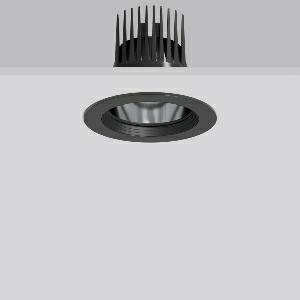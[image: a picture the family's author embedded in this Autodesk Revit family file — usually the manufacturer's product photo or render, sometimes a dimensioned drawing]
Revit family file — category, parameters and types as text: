
# Revit family: heledon_maxi_e_901787_003_2_76_4586
name_source: partatom
category: Lighting Fixtures
units: mm (PartAtom-declared; Revit-internal decimal feet)

## family parameters
Cut with Voids When Loaded = No
Host = Face
Light Source = No
Part Type = Normal
Room Calculation Point = No
Round Connector Dimension = Use Diameter
Shared = No

## types (1)
- HELEDON maxi E (1 x LED Modul 927 bakery, 3300 lm, 2700)
    Apparent Load = 33 VA
    Approval mark = CE
    CIE Flux Codes = 96 100 100 100 100
    Color Rendering = 90
    Color Temperature = 2700
    Default Elevation = 1800 mm
    Description = Series: HELEDON maxi
Round recessed downlight. Housing: die-cast aluminium, powder-coated. Black plastic ring and recessed LED to prevent glare from the side. Optical assembly with reflector made of MIRO-Silver with 98% total light reflection for outstanding efficiency - can be changed without tools. Special LED for illumination of pastries included. Suitable for Recessed ceiling mounting. Installation without tools thanks to spring fastening system. Including separate LED converter with connecting cable 600 mm.High quality converter without flickering and stroboscopic effect. Through-wiring box (5 pole) available as accessory. The following accessories can be mounted without use of tools: interchangeable lenses, decorative glasses, honeycomb louvre, clear and frosted diffusers, white interchangeable plastic ring. 
Colour: deep black, matt (RAL 9005)
Diameter: 162 mm
Height: 3 mm
Cut-out diameter: 152 mm
Recess height: 200 mm
Luminaire: recess height: 135 mm
Lamp: LED
Socket: without socket
Colour temperature: bakery
Colour rendering index (CRI): 97
System power: 33 W
Rated luminous flux: 3300 lm
Luminous efficiency: 100 lm/W
Control gear: Converter, dimmable, DALI
Protection class: II
Type of protection: IP 20
    Height = 0 mm  [stored 0 ft]
    Lamp = 1 x LED Modul 927 bakery
    Lamp Light Flux = 3300 lm
    Lamp count = 1
    Length = 162 mm
    Lifetime = 50000 h
    Luminous efficacy = 100 lm/W
    Manufacturer = RZB
    ModVariant = No
    Model = 901787.003.2.76
    Mounting Place = Ceiling
    Mounting Type = Recessed
    Number of Poles = 1
    OnlyDefault = Yes
    Power Factor = 1
    Product Name = HELEDON maxi E
    Product group = Recessed downlights
    ProductGroupID = 402
    Protection Class = Protection class II
    Protection Degree = IP 20
    RLX_Detail_Level = 1
    RLX_Emergency_Light_Flux = 0 lm
    RLX_Emergency_Type = 0
    RLX_Emergency_Type_DB = No
    RlxData = <blob elided: 124113 chars, md5=1c438442>
    Socket = socket
    Standby Power = 0 W
    System Light Flux = 3300 lm
    System Power = 33 W
    Type Comments = Product without accessories
    Type Image = 901662.003.jpg
    URL = http://relux.com
    VarID = ---
    Voltage = 230 V
    Voltage Range = 220-240 V
    Weight = 0.00 kg
    Width = 0 mm  [stored 0 ft]

note: [stored X ft] marks values corroborated as IEEE doubles in the binary element streams (Revit-internal decimal feet)

## geometry (parser evidence)
native form markers: Blend x4, Sweep x10
no freeform markers — native parametric forms only
